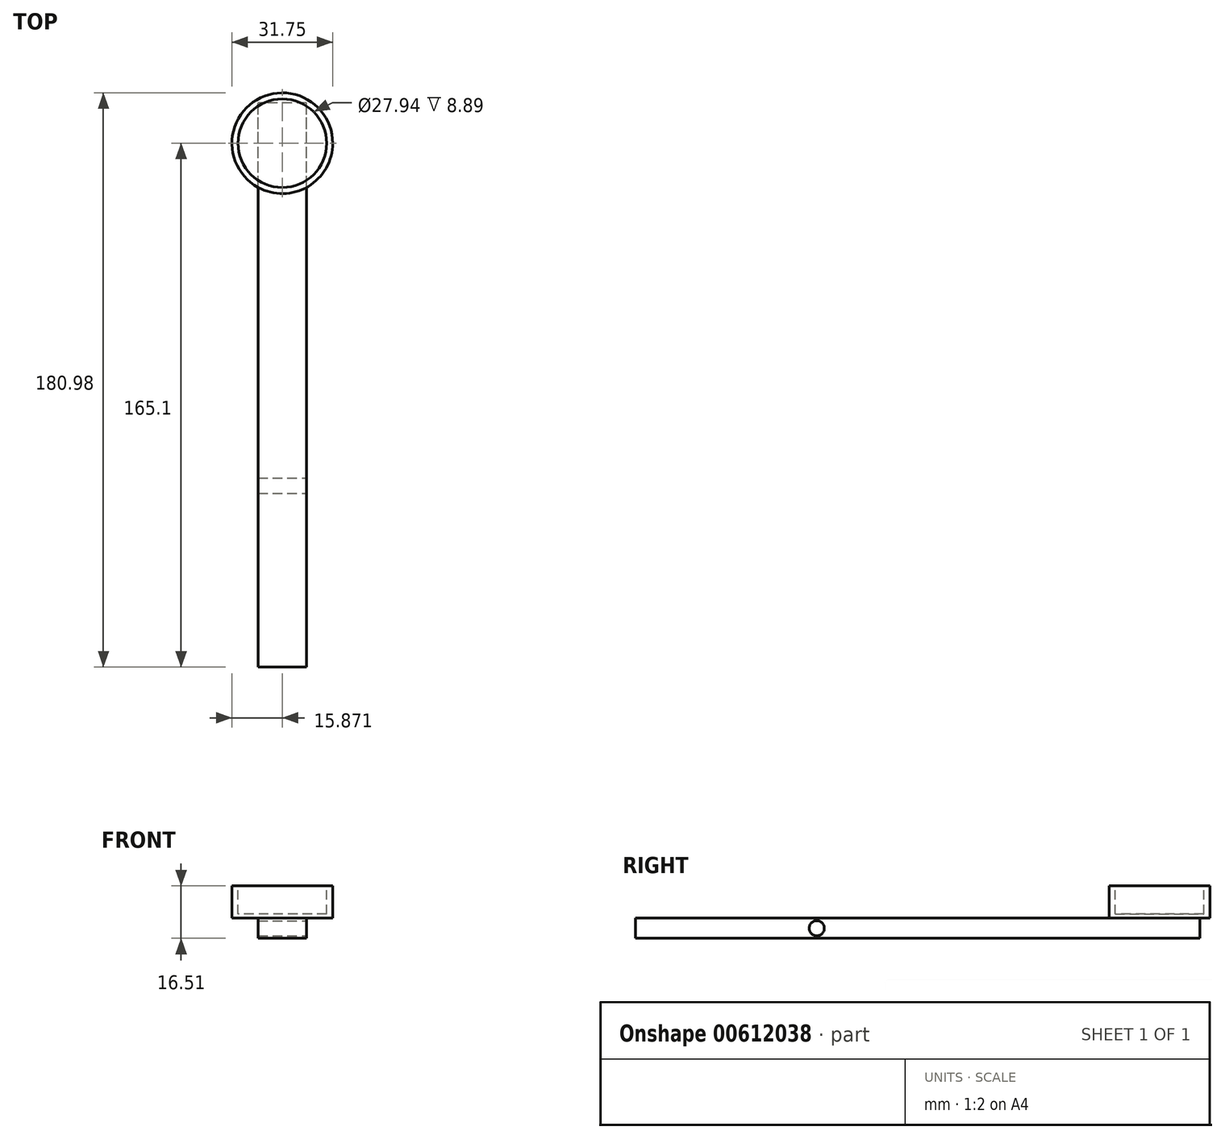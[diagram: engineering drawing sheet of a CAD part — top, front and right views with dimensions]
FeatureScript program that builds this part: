
annotation { "Feature Type Name" : "Feature", "Feature Type Description" : "" }
export const myFeature = defineFeature(function(context is Context, id is Id, definition is map)
    precondition{}
    {
        {
            var Q0;
            Q0=qCreatedBy(makeId("Front.planeOp"),FACE);
            var sketch = newSketch(context, id + "F0", { "sketchPlane" : qUnion([Q0])});
            skLineSegment(sketch, "E0", {"start": v(-5.97, 0.27) * mm, "end": v(9.27, 0.27) * mm});
            skLineSegment(sketch, "E1", {"start": v(9.27, 0.27) * mm, "end": v(9.27, -6.08) * mm});
            skLineSegment(sketch, "E2", {"start": v(9.27, -6.08) * mm, "end": v(-5.97, -6.08) * mm});
            skLineSegment(sketch, "E3", {"start": v(-5.97, -6.08) * mm, "end": v(-5.97, 0.27) * mm});
            skSolve(sketch);
        }
        {
            var Q0;
            Q0 = qSketchRegion(id + "F0", true);
            extrude(context, id + "F1", {"entities" : qUnion([Q0]), "depth" : 177.8 * mm, "offsetDistance" : 25.4 * mm});
        }
        {
            var Q0;
            Q0=makeQuery(id+"F1.opExtrude","SWEPT_FACE",FACE,{"disambiguationData":[OSD([sQuery(id+"F0.wireOp",EDGE,"E1")])]});
            var sketch = newSketch(context, id + "F2", { "sketchPlane" : qUnion([Q0])});
            skCircle(sketch, "E4", {"center": v(-120.65, -2.9) * mm, "radius": 2.39 * mm});
            skPoint(sketch, "E4.centerSnap0", {"position": v(-177.8, -2.9) * mm});
            skSolve(sketch);
        }
        {
            var Q0;
            Q0 = qSketchRegion(id + "F2", true);
            extrude(context, id + "F3", {"entities" : qUnion([Q0]), "operationType" : NewBodyOperationType.REMOVE, "endBound" : BoundingType.THROUGH_ALL, "oppositeDirection" : true, "depth" : 25.4 * mm, "offsetDistance" : 25.4 * mm});
        }
        {
            var Q0;
            Q0=makeQuery(id+"F1.opExtrude","SWEPT_FACE",FACE,{"disambiguationData":[OSD([sQuery(id+"F0.wireOp",EDGE,"E0")])]});
            var sketch = newSketch(context, id + "F4", { "sketchPlane" : qUnion([Q0])});
            skCircle(sketch, "E5", {"center": v(1.65, -12.7) * mm, "radius": 15.88 * mm});
            skPoint(sketch, "E5.centerSnap0", {"position": v(1.65, 0) * mm});
            skSolve(sketch);
        }
        {
            var Q0;
            Q0 = qSketchRegion(id + "F4", true);
            extrude(context, id + "F5", {"entities" : qUnion([Q0]), "operationType" : NewBodyOperationType.ADD, "depth" : 10.16 * mm, "offsetDistance" : 25.4 * mm});
        }
        {
            var Q0;
            Q0=makeQuery(id+"F5.opExtrude","CAP_FACE",FACE,{"disambiguationData":[OSD([sQuery(id+"F4.wireOp",EDGE,"E5")])],"isStart":false});
            var sketch = newSketch(context, id + "F6", { "sketchPlane" : qUnion([Q0])});
            skCircle(sketch, "E6", {"center": v(1.65, -12.7) * mm, "radius": 13.97 * mm});
            skSolve(sketch);
        }
        {
            var Q0;
            Q0 = qSketchRegion(id + "F6", true);
            extrude(context, id + "F7", {"entities" : qUnion([Q0]), "operationType" : NewBodyOperationType.REMOVE, "oppositeDirection" : true, "depth" : 8.9 * mm, "offsetDistance" : 25.4 * mm});
        }
    });
